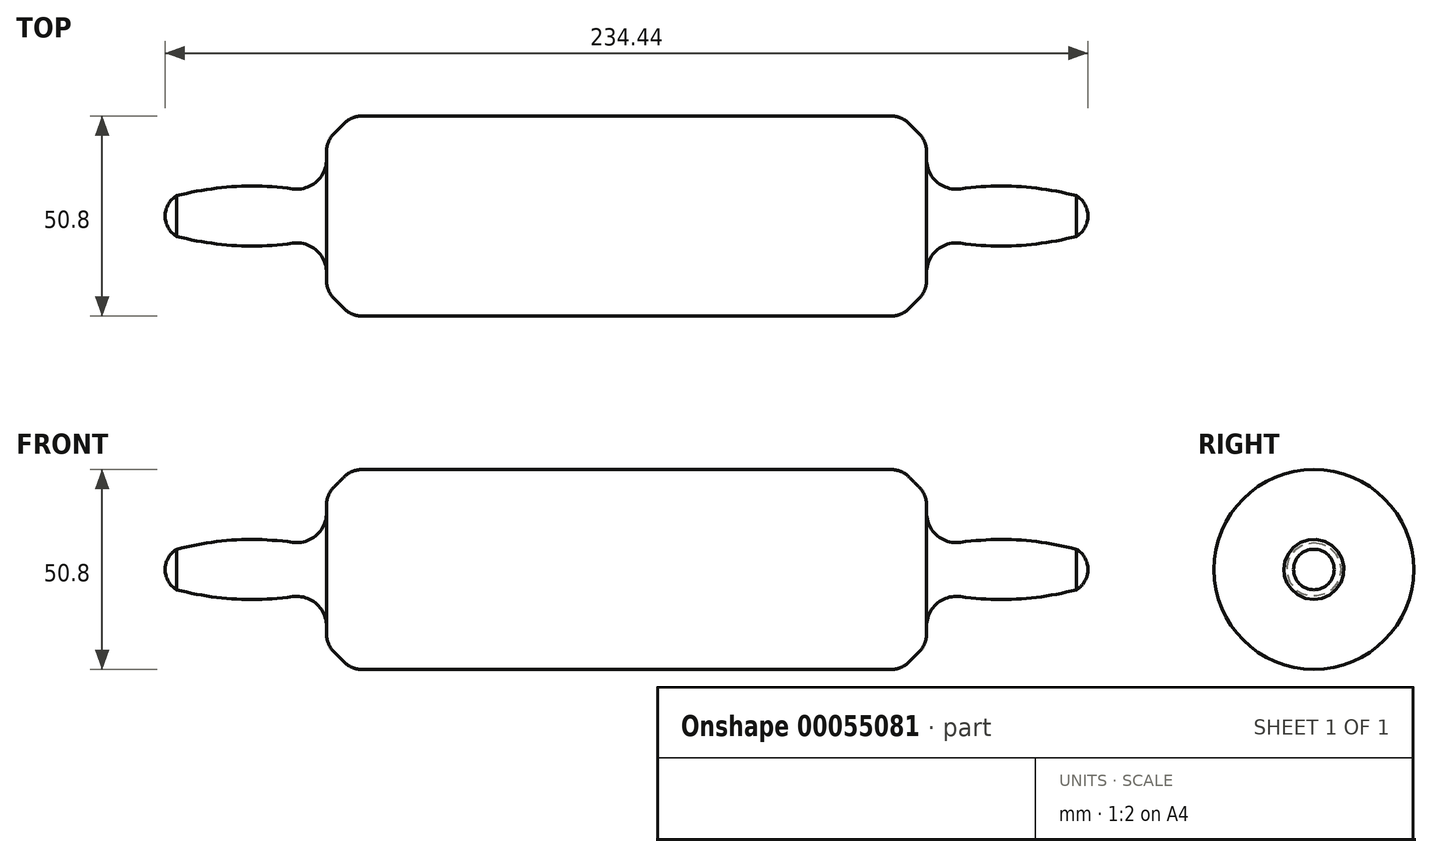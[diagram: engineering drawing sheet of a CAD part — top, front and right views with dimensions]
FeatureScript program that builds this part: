
annotation { "Feature Type Name" : "Feature", "Feature Type Description" : "" }
export const myFeature = defineFeature(function(context is Context, id is Id, definition is map)
    precondition{}
    {
        {
            var Q0;
            Q0=qCreatedBy(makeId("Front.planeOp"),FACE);
            var sketch = newSketch(context, id + "F0", { "sketchPlane" : qUnion([Q0])});
            skLineSegment(sketch, "E0.bottom", {"start": v(-78.4, 0) * mm, "end": v(74, 0) * mm});
            skLineSegment(sketch, "E0.top", {"start": v(-78.4, 25.4) * mm, "end": v(74, 25.4) * mm});
            skLineSegment(sketch, "E0.left", {"start": v(-78.4, 5.15) * mm, "end": v(-78.4, 25.4) * mm});
            skLineSegment(sketch, "E0.right", {"start": v(74, 5.15) * mm, "end": v(74, 25.4) * mm});
            skLineSegment(sketch, "E1", {"start": v(-78.4, 0) * mm, "end": v(-113.42, 0) * mm});
            skArc(sketch, "E2", {"start": v(-78.4, 5.15) * mm, "mid": v(-97.45, 7.62) * mm, "end": v(-116.5, 5.15) * mm});
            skArc(sketch, "E3", {"start": v(-116.5, 5.15) * mm, "mid": v(-118.64, 2.96) * mm, "end": v(-119.42, 0) * mm});
            skPoint(sketch, "E4.end.orphan", {"position": v(-116.5, 0) * mm});
            skLineSegment(sketch, "E5", {"start": v(-113.42, 0) * mm, "end": v(-119.42, 0) * mm});
            skArc(sketch, "E6.MirrorCS", {"start": v(74, 5.15) * mm, "mid": v(93.05, 7.62) * mm, "end": v(112.1, 5.15) * mm});
            skLineSegment(sketch, "E7.MirrorCS", {"start": v(74, 0) * mm, "end": v(109.02, 0) * mm});
            skArc(sketch, "E8.MirrorCS", {"start": v(112.1, 5.15) * mm, "mid": v(114.24, 2.96) * mm, "end": v(115.02, 0) * mm});
            skLineSegment(sketch, "E9.MirrorCS", {"start": v(109.02, 0) * mm, "end": v(115.02, 0) * mm});
            skPoint(sketch, "E10.start.orphan", {"position": v(-2.2, 25.4) * mm});
            skSolve(sketch);
        }
        {
            var Q0;
            Q0=makeQuery(id+"F0.imprint","IMPRINT",FACE,{"disambiguationData":[TD([[makeQuery(id+"F0.imprint","IMPRINT",EDGE,{"derivedFrom":sQuery(id+"F0.wireOp",EDGE,"E0.bottom")}),1.0]])]});
            var Q1;
            Q1=sQuery(id+"F0.wireOp",EDGE,"E0.bottom");
            revolve(context, id + "F1", {"entities" : qUnion([Q0]), "axis" : qUnion([Q1]), "revolveType" : RevolveType.FULL});
        }
        {
            var Q0;
            Q0=makeQuery(id+"F1.opRevolve","SWEPT_EDGE",EDGE,{"disambiguationData":[OSD([sQuery(id+"F0.wireOp",EDGE,"E0.top"),sQuery(id+"F0.wireOp",EDGE,"E0.right")])]});
            var Q1;
            Q1=makeQuery(id+"F1.opRevolve","SWEPT_EDGE",EDGE,{"disambiguationData":[OSD([sQuery(id+"F0.wireOp",EDGE,"E0.top"),sQuery(id+"F0.wireOp",EDGE,"E0.left")])]});
            chamfer(context, id + "F2", {"entities" : qUnion([Q0, Q1]), "width" : 6.35 * mm, "tangentPropagation" : true});
        }
        {
            var Q0;
            {var subQ0=sQuery(id+"F0.wireOp",EDGE,"E0.right");Q0=makeQuery(id+"F2.opChamfer","BLEND_EDGE",EDGE,{"blendedFrom":[makeQuery(id+"F1.opRevolve","SWEPT_EDGE",EDGE,{"disambiguationData":[OSD([sQuery(id+"F0.wireOp",EDGE,"E0.top"),subQ0])]}),makeQuery(id+"F1.opRevolve","SWEPT_FACE",FACE,{"disambiguationData":[OSD([subQ0])]})],"blendedInto":[makeQuery(id+"F1.opRevolve","SWEPT_FACE",FACE,{"disambiguationData":[OSD([subQ0])]})]});}
            var Q1;
            {var subQ0=sQuery(id+"F0.wireOp",EDGE,"E0.top");Q1=makeQuery(id+"F2.opChamfer","BLEND_EDGE",EDGE,{"blendedFrom":[makeQuery(id+"F1.opRevolve","SWEPT_EDGE",EDGE,{"disambiguationData":[OSD([subQ0,sQuery(id+"F0.wireOp",EDGE,"E0.right")])]}),makeQuery(id+"F1.opRevolve","SWEPT_FACE",FACE,{"disambiguationData":[OSD([subQ0])]})],"blendedInto":[makeQuery(id+"F1.opRevolve","SWEPT_FACE",FACE,{"disambiguationData":[OSD([subQ0])]})]});}
            var Q2;
            {var subQ0=sQuery(id+"F0.wireOp",EDGE,"E0.left");Q2=makeQuery(id+"F2.opChamfer","BLEND_EDGE",EDGE,{"blendedFrom":[makeQuery(id+"F1.opRevolve","SWEPT_EDGE",EDGE,{"disambiguationData":[OSD([sQuery(id+"F0.wireOp",EDGE,"E0.top"),subQ0])]}),makeQuery(id+"F1.opRevolve","SWEPT_FACE",FACE,{"disambiguationData":[OSD([subQ0])]})],"blendedInto":[makeQuery(id+"F1.opRevolve","SWEPT_FACE",FACE,{"disambiguationData":[OSD([subQ0])]})]});}
            var Q3;
            {var subQ0=sQuery(id+"F0.wireOp",EDGE,"E0.top");Q3=makeQuery(id+"F2.opChamfer","BLEND_EDGE",EDGE,{"blendedFrom":[makeQuery(id+"F1.opRevolve","SWEPT_EDGE",EDGE,{"disambiguationData":[OSD([subQ0,sQuery(id+"F0.wireOp",EDGE,"E0.left")])]}),makeQuery(id+"F1.opRevolve","SWEPT_FACE",FACE,{"disambiguationData":[OSD([subQ0])]})],"blendedInto":[makeQuery(id+"F1.opRevolve","SWEPT_FACE",FACE,{"disambiguationData":[OSD([subQ0])]})]});}
            fillet(context, id + "F3", {"entities" : qUnion([Q0, Q1, Q2, Q3]), "radius" : 6.35 * mm, "tangentPropagation" : true, "allowEdgeOverflow" : false});
        }
        {
            var Q0;
            Q0=makeQuery(id+"F1.opRevolve","SWEPT_EDGE",EDGE,{"disambiguationData":[OSD([sQuery(id+"F0.wireOp",EDGE,"E0.right"),sQuery(id+"F0.wireOp",EDGE,"E6.MirrorCS")])]});
            var Q1;
            Q1=makeQuery(id+"F1.opRevolve","SWEPT_EDGE",EDGE,{"disambiguationData":[OSD([sQuery(id+"F0.wireOp",EDGE,"E0.left"),sQuery(id+"F0.wireOp",EDGE,"E2")])]});
            fillet(context, id + "F4", {"entities" : qUnion([Q0, Q1]), "radius" : 7.62 * mm, "tangentPropagation" : true, "allowEdgeOverflow" : false});
        }
    });
